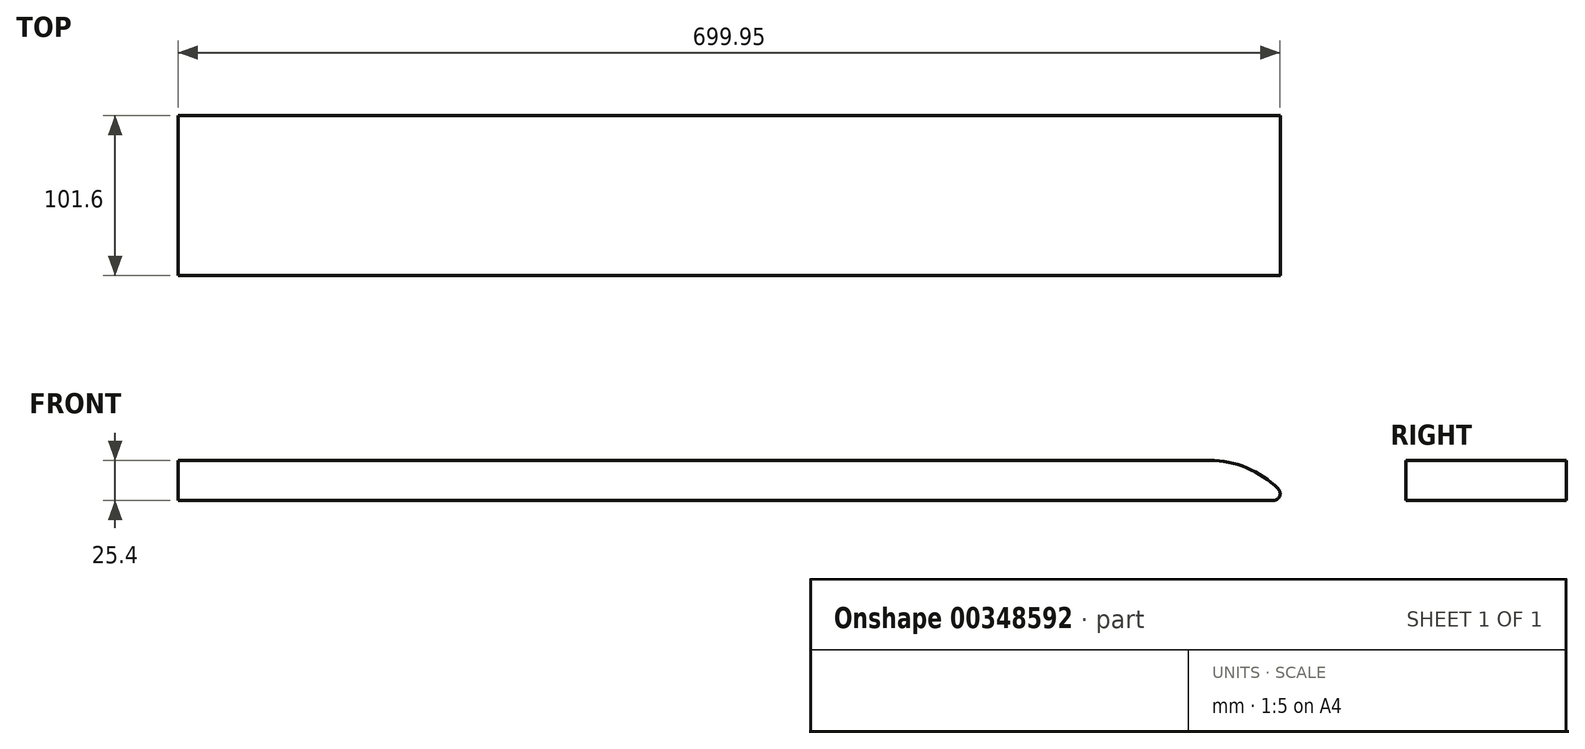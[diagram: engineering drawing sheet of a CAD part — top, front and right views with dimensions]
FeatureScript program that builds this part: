
annotation { "Feature Type Name" : "Feature", "Feature Type Description" : "" }
export const myFeature = defineFeature(function(context is Context, id is Id, definition is map)
    precondition{}
    {
        {
            var Q0;
            Q0=qCreatedBy(makeId("Top.planeOp"),FACE);
            var sketch = newSketch(context, id + "F0", { "sketchPlane" : qUnion([Q0])});
            skLineSegment(sketch, "E0.bottom", {"start": v(-326.86, 62.77) * mm, "end": v(378, 62.77) * mm});
            skLineSegment(sketch, "E0.top", {"start": v(-326.86, -38.83) * mm, "end": v(378, -38.83) * mm});
            skLineSegment(sketch, "E0.left", {"start": v(-326.86, 62.77) * mm, "end": v(-326.86, -38.83) * mm});
            skLineSegment(sketch, "E0.right", {"start": v(378, 62.77) * mm, "end": v(378, -38.83) * mm});
            skSolve(sketch);
        }
        {
            var Q0;
            Q0 = qSketchRegion(id + "F0", true);
            extrude(context, id + "F1", {"entities" : qUnion([Q0]), "depth" : 25.4 * mm});
        }
        {
            var Q0;
            Q0=makeQuery(id+"F1.opExtrude","CAP_EDGE",EDGE,{"disambiguationData":[OSD([sQuery(id+"F0.wireOp",EDGE,"E0.right")])],"isStart":false});
            fillet(context, id + "F2", {"entities" : qUnion([Q0]), "radius" : 61.32 * mm, "tangentPropagation" : true, "allowEdgeOverflow" : false});
        }
        {
            var Q0;
            {var subQ0=sQuery(id+"F0.wireOp",EDGE,"E0.right");Q0=makeQuery(id+"F2.opFillet","BLEND_EDGE",EDGE,{"blendedFrom":[makeQuery(id+"F1.opExtrude","CAP_EDGE",EDGE,{"disambiguationData":[OSD([subQ0])],"isStart":false}),makeQuery(id+"F1.opExtrude","CAP_FACE",FACE,{"disambiguationData":[OSD([sQuery(id+"F0.wireOp",EDGE,"E0.bottom"),sQuery(id+"F0.wireOp",EDGE,"E0.top"),sQuery(id+"F0.wireOp",EDGE,"E0.left"),subQ0])],"isStart":true})],"blendedInto":[makeQuery(id+"F1.opExtrude","CAP_FACE",FACE,{"disambiguationData":[OSD([sQuery(id+"F0.wireOp",EDGE,"E0.bottom"),sQuery(id+"F0.wireOp",EDGE,"E0.top"),sQuery(id+"F0.wireOp",EDGE,"E0.left"),subQ0])],"isStart":true})]});}
            fillet(context, id + "F3", {"entities" : qUnion([Q0]), "radius" : 4.24 * mm, "tangentPropagation" : true, "allowEdgeOverflow" : false});
        }
    });
